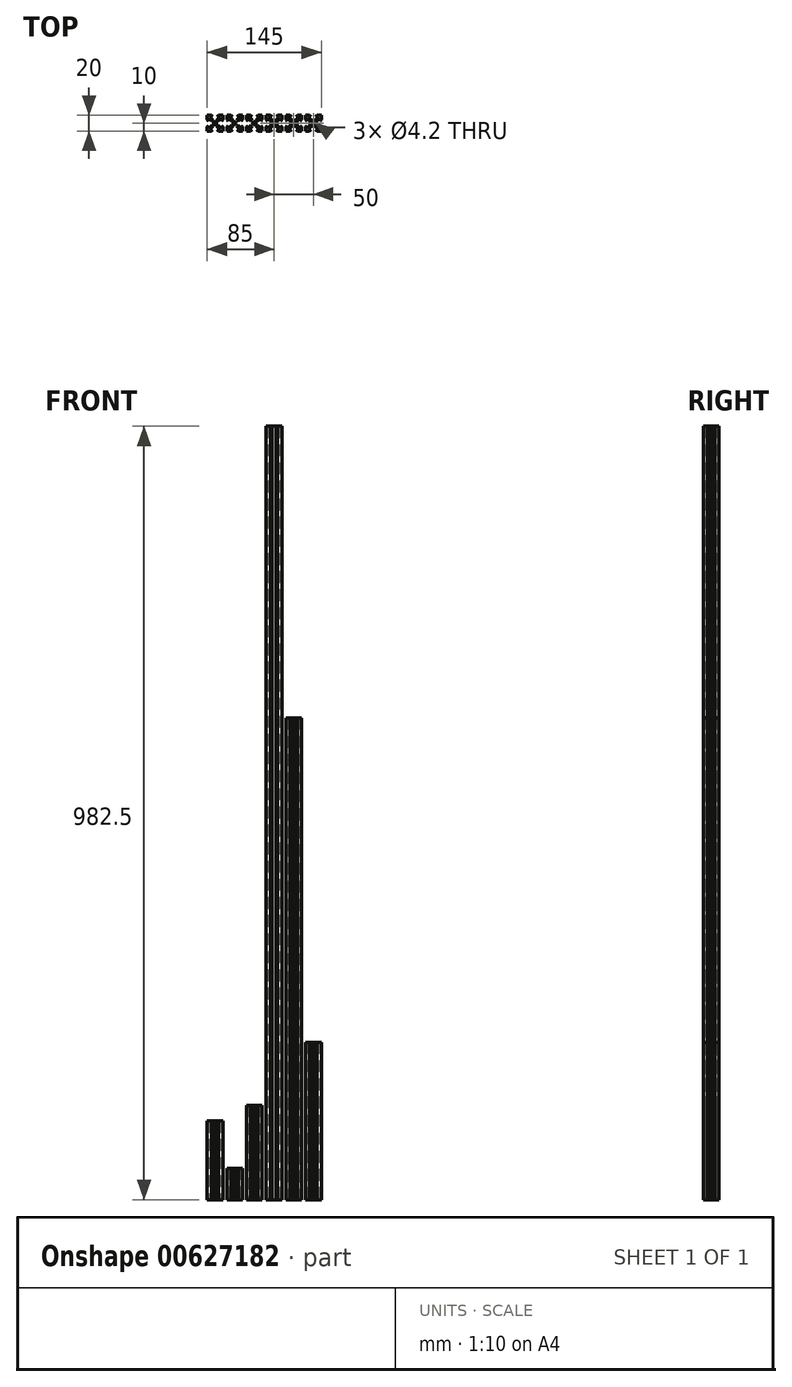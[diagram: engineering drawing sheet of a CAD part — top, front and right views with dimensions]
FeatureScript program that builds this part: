
annotation { "Feature Type Name" : "Feature", "Feature Type Description" : "" }
export const myFeature = defineFeature(function(context is Context, id is Id, definition is map)
    precondition{}
    {
        {
            var Q0;
            Q0=qCreatedBy(makeId("Top.planeOp"),FACE);
            var sketch = newSketch(context, id + "F0", { "sketchPlane" : qUnion([Q0])});
            skLineSegment(sketch, "E0.bottom", {"start": v(10, -10) * mm, "end": v(-10, -10) * mm});
            skLineSegment(sketch, "E0.top", {"start": v(10, 10) * mm, "end": v(-10, 10) * mm});
            skLineSegment(sketch, "E0.left", {"start": v(10, -10) * mm, "end": v(10, 10) * mm});
            skLineSegment(sketch, "E0.right", {"start": v(-10, -10) * mm, "end": v(-10, 10) * mm});
            skPoint(sketch, "E0.middle", {"position": v(0, 0) * mm});
            skCircle(sketch, "E1", {"center": v(0, 0) * mm, "radius": 2.1 * mm});
            skLineSegment(sketch, "E2.bottom", {"start": v(8.2, -8.2) * mm, "end": v(-8.2, -8.2) * mm});
            skLineSegment(sketch, "E2.top", {"start": v(8.2, 8.2) * mm, "end": v(-8.2, 8.2) * mm});
            skLineSegment(sketch, "E2.left", {"start": v(8.2, -8.2) * mm, "end": v(8.2, 8.2) * mm});
            skLineSegment(sketch, "E2.right", {"start": v(-8.2, -8.2) * mm, "end": v(-8.2, 8.2) * mm});
            skLineSegment(sketch, "E3", {"start": v(-8.2, 2.84) * mm, "end": v(-8.2, -2.84) * mm});
            skLineSegment(sketch, "E4", {"start": v(-8.2, 2.84) * mm, "end": v(-10, 4.64) * mm});
            skLineSegment(sketch, "E5", {"start": v(-10, 10) * mm, "end": v(10, -10) * mm, "construction": true});
            skLineSegment(sketch, "E6", {"start": v(10, 10) * mm, "end": v(-10, -10) * mm, "construction": true});
            skLineSegment(sketch, "E7", {"start": v(0, 10) * mm, "end": v(0, -10) * mm, "construction": true});
            skLineSegment(sketch, "E8", {"start": v(10, 0) * mm, "end": v(-10, 0) * mm, "construction": true});
            skLineSegment(sketch, "E9.MirrorCS", {"start": v(-2.84, 8.2) * mm, "end": v(-4.64, 10) * mm});
            skLineSegment(sketch, "E10.MirrorCS", {"start": v(2.84, -8.2) * mm, "end": v(4.64, -10) * mm});
            skLineSegment(sketch, "E11.MirrorCS", {"start": v(8.2, -2.84) * mm, "end": v(10, -4.64) * mm});
            skLineSegment(sketch, "E12.MirrorCS", {"start": v(2.84, 8.2) * mm, "end": v(4.64, 10) * mm});
            skLineSegment(sketch, "E13.MirrorCS", {"start": v(8.2, 2.84) * mm, "end": v(10, 4.64) * mm});
            skLineSegment(sketch, "E14.MirrorCS", {"start": v(-8.2, -2.84) * mm, "end": v(-10, -4.64) * mm});
            skLineSegment(sketch, "E15.MirrorCS", {"start": v(-2.84, -8.2) * mm, "end": v(-4.64, -10) * mm});
            skLineSegment(sketch, "E16.bottom", {"start": v(4, -4) * mm, "end": v(-4, -4) * mm});
            skLineSegment(sketch, "E16.top", {"start": v(4, 4) * mm, "end": v(-4, 4) * mm});
            skLineSegment(sketch, "E16.left", {"start": v(4, -4) * mm, "end": v(4, 4) * mm});
            skLineSegment(sketch, "E16.right", {"start": v(-4, -4) * mm, "end": v(-4, 4) * mm});
            skLineSegment(sketch, "E17", {"start": v(6.5, 8.2) * mm, "end": v(2.3, 4) * mm});
            skLineSegment(sketch, "E18.MirrorCS", {"start": v(8.2, 6.5) * mm, "end": v(4, 2.3) * mm});
            skLineSegment(sketch, "E19.MirrorCS", {"start": v(8.2, -6.5) * mm, "end": v(4, -2.3) * mm});
            skLineSegment(sketch, "E20.MirrorCS", {"start": v(6.5, -8.2) * mm, "end": v(2.3, -4) * mm});
            skLineSegment(sketch, "E21.MirrorCS", {"start": v(-6.5, -8.2) * mm, "end": v(-2.3, -4) * mm});
            skLineSegment(sketch, "E22.MirrorCS", {"start": v(-8.2, -6.5) * mm, "end": v(-4, -2.3) * mm});
            skLineSegment(sketch, "E23.MirrorCS", {"start": v(-6.5, 8.2) * mm, "end": v(-2.3, 4) * mm});
            skLineSegment(sketch, "E24.MirrorCS", {"start": v(-8.2, 6.5) * mm, "end": v(-4, 2.3) * mm});
            skLineSegment(sketch, "E25.1.0.0", {"start": v(33.2, 6.5) * mm, "end": v(29, 2.3) * mm});
            skLineSegment(sketch, "E25.1.0.1", {"start": v(35, -10) * mm, "end": v(15, -10) * mm});
            skLineSegment(sketch, "E25.1.0.2", {"start": v(15, -10) * mm, "end": v(15, 10) * mm});
            skLineSegment(sketch, "E25.1.0.3", {"start": v(18.5, -8.2) * mm, "end": v(22.7, -4) * mm});
            skLineSegment(sketch, "E25.1.0.4", {"start": v(21, -4) * mm, "end": v(21, 4) * mm});
            skLineSegment(sketch, "E25.1.0.5", {"start": v(16.8, 6.5) * mm, "end": v(21, 2.3) * mm});
            skPoint(sketch, "E25.1.0.6", {"position": v(25, 0) * mm});
            skLineSegment(sketch, "E25.1.0.7", {"start": v(16.8, -6.5) * mm, "end": v(21, -2.3) * mm});
            skLineSegment(sketch, "E25.1.0.8", {"start": v(25, 10) * mm, "end": v(25, -10) * mm, "construction": true});
            skLineSegment(sketch, "E25.1.0.9", {"start": v(35, -10) * mm, "end": v(35, 10) * mm});
            skLineSegment(sketch, "E25.1.0.10", {"start": v(35, 0) * mm, "end": v(15, 0) * mm, "construction": true});
            skLineSegment(sketch, "E25.1.0.11", {"start": v(35, 10) * mm, "end": v(15, 10) * mm});
            skLineSegment(sketch, "E25.1.0.12", {"start": v(16.8, -8.2) * mm, "end": v(16.8, 8.2) * mm});
            skLineSegment(sketch, "E25.1.0.13", {"start": v(33.2, 8.2) * mm, "end": v(16.8, 8.2) * mm});
            skLineSegment(sketch, "E25.1.0.14", {"start": v(16.8, -2.84) * mm, "end": v(15, -4.64) * mm});
            skLineSegment(sketch, "E25.1.0.15", {"start": v(18.5, 8.2) * mm, "end": v(22.7, 4) * mm});
            skLineSegment(sketch, "E25.1.0.16", {"start": v(29, 4) * mm, "end": v(21, 4) * mm});
            skLineSegment(sketch, "E25.1.0.17", {"start": v(33.2, -8.2) * mm, "end": v(33.2, 8.2) * mm});
            skLineSegment(sketch, "E25.1.0.18", {"start": v(16.8, 2.84) * mm, "end": v(16.8, -2.84) * mm});
            skLineSegment(sketch, "E25.1.0.19", {"start": v(29, -4) * mm, "end": v(29, 4) * mm});
            skLineSegment(sketch, "E25.1.0.20", {"start": v(33.2, -8.2) * mm, "end": v(16.8, -8.2) * mm});
            skLineSegment(sketch, "E25.1.0.21", {"start": v(35, 10) * mm, "end": v(15, -10) * mm, "construction": true});
            skLineSegment(sketch, "E25.1.0.22", {"start": v(33.2, -2.84) * mm, "end": v(35, -4.64) * mm});
            skLineSegment(sketch, "E25.1.0.23", {"start": v(31.5, -8.2) * mm, "end": v(27.3, -4) * mm});
            skCircle(sketch, "E25.1.0.24", {"center": v(25, 0) * mm, "radius": 2.1 * mm});
            skLineSegment(sketch, "E25.1.0.25", {"start": v(33.2, -6.5) * mm, "end": v(29, -2.3) * mm});
            skLineSegment(sketch, "E25.1.0.26", {"start": v(31.5, 8.2) * mm, "end": v(27.3, 4) * mm});
            skLineSegment(sketch, "E25.1.0.27", {"start": v(15, 10) * mm, "end": v(35, -10) * mm, "construction": true});
            skLineSegment(sketch, "E25.1.0.28", {"start": v(29, -4) * mm, "end": v(21, -4) * mm});
            skLineSegment(sketch, "E25.1.0.29", {"start": v(33.2, 2.84) * mm, "end": v(35, 4.64) * mm});
            skLineSegment(sketch, "E25.1.0.30", {"start": v(16.8, 2.84) * mm, "end": v(15, 4.64) * mm});
            skLineSegment(sketch, "E25.1.0.31", {"start": v(27.84, 8.2) * mm, "end": v(29.64, 10) * mm});
            skLineSegment(sketch, "E25.1.0.32", {"start": v(22.16, 8.2) * mm, "end": v(20.36, 10) * mm});
            skLineSegment(sketch, "E25.1.0.33", {"start": v(27.84, -8.2) * mm, "end": v(29.64, -10) * mm});
            skLineSegment(sketch, "E25.1.0.34", {"start": v(22.16, -8.2) * mm, "end": v(20.36, -10) * mm});
            skPoint(sketch, "E25.1.0.35", {"position": v(25, 0) * mm});
            skPoint(sketch, "E25.1.0.36", {"position": v(25, 0) * mm});
            skLineSegment(sketch, "E25.2.0.0", {"start": v(58.2, 6.5) * mm, "end": v(54, 2.3) * mm});
            skLineSegment(sketch, "E25.2.0.1", {"start": v(60, -10) * mm, "end": v(40, -10) * mm});
            skLineSegment(sketch, "E25.2.0.2", {"start": v(40, -10) * mm, "end": v(40, 10) * mm});
            skLineSegment(sketch, "E25.2.0.3", {"start": v(43.5, -8.2) * mm, "end": v(47.7, -4) * mm});
            skLineSegment(sketch, "E25.2.0.4", {"start": v(46, -4) * mm, "end": v(46, 4) * mm});
            skLineSegment(sketch, "E25.2.0.5", {"start": v(41.8, 6.5) * mm, "end": v(46, 2.3) * mm});
            skPoint(sketch, "E25.2.0.6", {"position": v(50, 0) * mm});
            skLineSegment(sketch, "E25.2.0.7", {"start": v(41.8, -6.5) * mm, "end": v(46, -2.3) * mm});
            skLineSegment(sketch, "E25.2.0.8", {"start": v(50, 10) * mm, "end": v(50, -10) * mm, "construction": true});
            skLineSegment(sketch, "E25.2.0.9", {"start": v(60, -10) * mm, "end": v(60, 10) * mm});
            skLineSegment(sketch, "E25.2.0.10", {"start": v(60, 0) * mm, "end": v(40, 0) * mm, "construction": true});
            skLineSegment(sketch, "E25.2.0.11", {"start": v(60, 10) * mm, "end": v(40, 10) * mm});
            skLineSegment(sketch, "E25.2.0.12", {"start": v(41.8, -8.2) * mm, "end": v(41.8, 8.2) * mm});
            skLineSegment(sketch, "E25.2.0.13", {"start": v(58.2, 8.2) * mm, "end": v(41.8, 8.2) * mm});
            skLineSegment(sketch, "E25.2.0.14", {"start": v(41.8, -2.84) * mm, "end": v(40, -4.64) * mm});
            skLineSegment(sketch, "E25.2.0.15", {"start": v(43.5, 8.2) * mm, "end": v(47.7, 4) * mm});
            skLineSegment(sketch, "E25.2.0.16", {"start": v(54, 4) * mm, "end": v(46, 4) * mm});
            skLineSegment(sketch, "E25.2.0.17", {"start": v(58.2, -8.2) * mm, "end": v(58.2, 8.2) * mm});
            skLineSegment(sketch, "E25.2.0.18", {"start": v(41.8, 2.84) * mm, "end": v(41.8, -2.84) * mm});
            skLineSegment(sketch, "E25.2.0.19", {"start": v(54, -4) * mm, "end": v(54, 4) * mm});
            skLineSegment(sketch, "E25.2.0.20", {"start": v(58.2, -8.2) * mm, "end": v(41.8, -8.2) * mm});
            skLineSegment(sketch, "E25.2.0.21", {"start": v(60, 10) * mm, "end": v(40, -10) * mm, "construction": true});
            skLineSegment(sketch, "E25.2.0.22", {"start": v(58.2, -2.84) * mm, "end": v(60, -4.64) * mm});
            skLineSegment(sketch, "E25.2.0.23", {"start": v(56.5, -8.2) * mm, "end": v(52.3, -4) * mm});
            skCircle(sketch, "E25.2.0.24", {"center": v(50, 0) * mm, "radius": 2.1 * mm});
            skLineSegment(sketch, "E25.2.0.25", {"start": v(58.2, -6.5) * mm, "end": v(54, -2.3) * mm});
            skLineSegment(sketch, "E25.2.0.26", {"start": v(56.5, 8.2) * mm, "end": v(52.3, 4) * mm});
            skLineSegment(sketch, "E25.2.0.27", {"start": v(40, 10) * mm, "end": v(60, -10) * mm, "construction": true});
            skLineSegment(sketch, "E25.2.0.28", {"start": v(54, -4) * mm, "end": v(46, -4) * mm});
            skLineSegment(sketch, "E25.2.0.29", {"start": v(58.2, 2.84) * mm, "end": v(60, 4.64) * mm});
            skLineSegment(sketch, "E25.2.0.30", {"start": v(41.8, 2.84) * mm, "end": v(40, 4.64) * mm});
            skLineSegment(sketch, "E25.2.0.31", {"start": v(52.84, 8.2) * mm, "end": v(54.64, 10) * mm});
            skLineSegment(sketch, "E25.2.0.32", {"start": v(47.16, 8.2) * mm, "end": v(45.36, 10) * mm});
            skLineSegment(sketch, "E25.2.0.33", {"start": v(52.84, -8.2) * mm, "end": v(54.64, -10) * mm});
            skLineSegment(sketch, "E25.2.0.34", {"start": v(47.16, -8.2) * mm, "end": v(45.36, -10) * mm});
            skPoint(sketch, "E25.2.0.35", {"position": v(50, 0) * mm});
            skPoint(sketch, "E25.2.0.36", {"position": v(50, 0) * mm});
            skLineSegment(sketch, "E25.3.0.0", {"start": v(83.2, 6.5) * mm, "end": v(79, 2.3) * mm});
            skLineSegment(sketch, "E25.3.0.1", {"start": v(85, -10) * mm, "end": v(65, -10) * mm});
            skLineSegment(sketch, "E25.3.0.2", {"start": v(65, -10) * mm, "end": v(65, 10) * mm});
            skLineSegment(sketch, "E25.3.0.3", {"start": v(68.5, -8.2) * mm, "end": v(72.7, -4) * mm});
            skLineSegment(sketch, "E25.3.0.4", {"start": v(71, -4) * mm, "end": v(71, 4) * mm});
            skLineSegment(sketch, "E25.3.0.5", {"start": v(66.8, 6.5) * mm, "end": v(71, 2.3) * mm});
            skPoint(sketch, "E25.3.0.6", {"position": v(75, 0) * mm});
            skLineSegment(sketch, "E25.3.0.7", {"start": v(66.8, -6.5) * mm, "end": v(71, -2.3) * mm});
            skLineSegment(sketch, "E25.3.0.8", {"start": v(75, 10) * mm, "end": v(75, -10) * mm, "construction": true});
            skLineSegment(sketch, "E25.3.0.9", {"start": v(85, -10) * mm, "end": v(85, 10) * mm});
            skLineSegment(sketch, "E25.3.0.10", {"start": v(85, 0) * mm, "end": v(65, 0) * mm, "construction": true});
            skLineSegment(sketch, "E25.3.0.11", {"start": v(85, 10) * mm, "end": v(65, 10) * mm});
            skLineSegment(sketch, "E25.3.0.12", {"start": v(66.8, -8.2) * mm, "end": v(66.8, 8.2) * mm});
            skLineSegment(sketch, "E25.3.0.13", {"start": v(83.2, 8.2) * mm, "end": v(66.8, 8.2) * mm});
            skLineSegment(sketch, "E25.3.0.14", {"start": v(66.8, -2.84) * mm, "end": v(65, -4.64) * mm});
            skLineSegment(sketch, "E25.3.0.15", {"start": v(68.5, 8.2) * mm, "end": v(72.7, 4) * mm});
            skLineSegment(sketch, "E25.3.0.16", {"start": v(79, 4) * mm, "end": v(71, 4) * mm});
            skLineSegment(sketch, "E25.3.0.17", {"start": v(83.2, -8.2) * mm, "end": v(83.2, 8.2) * mm});
            skLineSegment(sketch, "E25.3.0.18", {"start": v(66.8, 2.84) * mm, "end": v(66.8, -2.84) * mm});
            skLineSegment(sketch, "E25.3.0.19", {"start": v(79, -4) * mm, "end": v(79, 4) * mm});
            skLineSegment(sketch, "E25.3.0.20", {"start": v(83.2, -8.2) * mm, "end": v(66.8, -8.2) * mm});
            skLineSegment(sketch, "E25.3.0.21", {"start": v(85, 10) * mm, "end": v(65, -10) * mm, "construction": true});
            skLineSegment(sketch, "E25.3.0.22", {"start": v(83.2, -2.84) * mm, "end": v(85, -4.64) * mm});
            skLineSegment(sketch, "E25.3.0.23", {"start": v(81.5, -8.2) * mm, "end": v(77.3, -4) * mm});
            skCircle(sketch, "E25.3.0.24", {"center": v(75, 0) * mm, "radius": 2.1 * mm});
            skLineSegment(sketch, "E25.3.0.25", {"start": v(83.2, -6.5) * mm, "end": v(79, -2.3) * mm});
            skLineSegment(sketch, "E25.3.0.26", {"start": v(81.5, 8.2) * mm, "end": v(77.3, 4) * mm});
            skLineSegment(sketch, "E25.3.0.27", {"start": v(65, 10) * mm, "end": v(85, -10) * mm, "construction": true});
            skLineSegment(sketch, "E25.3.0.28", {"start": v(79, -4) * mm, "end": v(71, -4) * mm});
            skLineSegment(sketch, "E25.3.0.29", {"start": v(83.2, 2.84) * mm, "end": v(85, 4.64) * mm});
            skLineSegment(sketch, "E25.3.0.30", {"start": v(66.8, 2.84) * mm, "end": v(65, 4.64) * mm});
            skLineSegment(sketch, "E25.3.0.31", {"start": v(77.84, 8.2) * mm, "end": v(79.64, 10) * mm});
            skLineSegment(sketch, "E25.3.0.32", {"start": v(72.16, 8.2) * mm, "end": v(70.36, 10) * mm});
            skLineSegment(sketch, "E25.3.0.33", {"start": v(77.84, -8.2) * mm, "end": v(79.64, -10) * mm});
            skLineSegment(sketch, "E25.3.0.34", {"start": v(72.16, -8.2) * mm, "end": v(70.36, -10) * mm});
            skPoint(sketch, "E25.3.0.35", {"position": v(75, 0) * mm});
            skPoint(sketch, "E25.3.0.36", {"position": v(75, 0) * mm});
            skLineSegment(sketch, "E25.4.0.0", {"start": v(108.2, 6.5) * mm, "end": v(104, 2.3) * mm});
            skLineSegment(sketch, "E25.4.0.1", {"start": v(110, -10) * mm, "end": v(90, -10) * mm});
            skLineSegment(sketch, "E25.4.0.2", {"start": v(90, -10) * mm, "end": v(90, 10) * mm});
            skLineSegment(sketch, "E25.4.0.3", {"start": v(93.5, -8.2) * mm, "end": v(97.7, -4) * mm});
            skLineSegment(sketch, "E25.4.0.4", {"start": v(96, -4) * mm, "end": v(96, 4) * mm});
            skLineSegment(sketch, "E25.4.0.5", {"start": v(91.8, 6.5) * mm, "end": v(96, 2.3) * mm});
            skPoint(sketch, "E25.4.0.6", {"position": v(100, 0) * mm});
            skLineSegment(sketch, "E25.4.0.7", {"start": v(91.8, -6.5) * mm, "end": v(96, -2.3) * mm});
            skLineSegment(sketch, "E25.4.0.8", {"start": v(100, 10) * mm, "end": v(100, -10) * mm, "construction": true});
            skLineSegment(sketch, "E25.4.0.9", {"start": v(110, -10) * mm, "end": v(110, 10) * mm});
            skLineSegment(sketch, "E25.4.0.10", {"start": v(110, 0) * mm, "end": v(90, 0) * mm, "construction": true});
            skLineSegment(sketch, "E25.4.0.11", {"start": v(110, 10) * mm, "end": v(90, 10) * mm});
            skLineSegment(sketch, "E25.4.0.12", {"start": v(91.8, -8.2) * mm, "end": v(91.8, 8.2) * mm});
            skLineSegment(sketch, "E25.4.0.13", {"start": v(108.2, 8.2) * mm, "end": v(91.8, 8.2) * mm});
            skLineSegment(sketch, "E25.4.0.14", {"start": v(91.8, -2.84) * mm, "end": v(90, -4.64) * mm});
            skLineSegment(sketch, "E25.4.0.15", {"start": v(93.5, 8.2) * mm, "end": v(97.7, 4) * mm});
            skLineSegment(sketch, "E25.4.0.16", {"start": v(104, 4) * mm, "end": v(96, 4) * mm});
            skLineSegment(sketch, "E25.4.0.17", {"start": v(108.2, -8.2) * mm, "end": v(108.2, 8.2) * mm});
            skLineSegment(sketch, "E25.4.0.18", {"start": v(91.8, 2.84) * mm, "end": v(91.8, -2.84) * mm});
            skLineSegment(sketch, "E25.4.0.19", {"start": v(104, -4) * mm, "end": v(104, 4) * mm});
            skLineSegment(sketch, "E25.4.0.20", {"start": v(108.2, -8.2) * mm, "end": v(91.8, -8.2) * mm});
            skLineSegment(sketch, "E25.4.0.21", {"start": v(110, 10) * mm, "end": v(90, -10) * mm, "construction": true});
            skLineSegment(sketch, "E25.4.0.22", {"start": v(108.2, -2.84) * mm, "end": v(110, -4.64) * mm});
            skLineSegment(sketch, "E25.4.0.23", {"start": v(106.5, -8.2) * mm, "end": v(102.3, -4) * mm});
            skCircle(sketch, "E25.4.0.24", {"center": v(100, 0) * mm, "radius": 2.1 * mm});
            skLineSegment(sketch, "E25.4.0.25", {"start": v(108.2, -6.5) * mm, "end": v(104, -2.3) * mm});
            skLineSegment(sketch, "E25.4.0.26", {"start": v(106.5, 8.2) * mm, "end": v(102.3, 4) * mm});
            skLineSegment(sketch, "E25.4.0.27", {"start": v(90, 10) * mm, "end": v(110, -10) * mm, "construction": true});
            skLineSegment(sketch, "E25.4.0.28", {"start": v(104, -4) * mm, "end": v(96, -4) * mm});
            skLineSegment(sketch, "E25.4.0.29", {"start": v(108.2, 2.84) * mm, "end": v(110, 4.64) * mm});
            skLineSegment(sketch, "E25.4.0.30", {"start": v(91.8, 2.84) * mm, "end": v(90, 4.64) * mm});
            skLineSegment(sketch, "E25.4.0.31", {"start": v(102.84, 8.2) * mm, "end": v(104.64, 10) * mm});
            skLineSegment(sketch, "E25.4.0.32", {"start": v(97.16, 8.2) * mm, "end": v(95.36, 10) * mm});
            skLineSegment(sketch, "E25.4.0.33", {"start": v(102.84, -8.2) * mm, "end": v(104.64, -10) * mm});
            skLineSegment(sketch, "E25.4.0.34", {"start": v(97.16, -8.2) * mm, "end": v(95.36, -10) * mm});
            skPoint(sketch, "E25.4.0.35", {"position": v(100, 0) * mm});
            skPoint(sketch, "E25.4.0.36", {"position": v(100, 0) * mm});
            skLineSegment(sketch, "E25.direction1", {"start": v(-10, -10) * mm, "end": v(15, -10) * mm, "construction": true});
            skLineSegment(sketch, "E26", {"start": v(-12.5, 5) * mm, "end": v(-12.5, -5) * mm, "construction": true});
            skLineSegment(sketch, "E27.MirrorCS", {"start": v(-16.8, -2.84) * mm, "end": v(-15, -4.64) * mm});
            skCircle(sketch, "E28.MirrorC", {"center": v(-50, 0) * mm, "radius": 2.1 * mm});
            skCircle(sketch, "E29.MirrorC", {"center": v(-125, 0) * mm, "radius": 2.1 * mm});
            skCircle(sketch, "E30.MirrorC", {"center": v(-25, 0) * mm, "radius": 2.1 * mm});
            skCircle(sketch, "E31.MirrorC", {"center": v(-100, 0) * mm, "radius": 2.1 * mm});
            skCircle(sketch, "E32.MirrorC", {"center": v(-75, 0) * mm, "radius": 2.1 * mm});
            skLineSegment(sketch, "E33.MirrorCS", {"start": v(-66.8, 2.84) * mm, "end": v(-66.8, -2.84) * mm});
            skLineSegment(sketch, "E34.MirrorCS", {"start": v(-91.8, 2.84) * mm, "end": v(-90, 4.64) * mm});
            skLineSegment(sketch, "E35.MirrorCS", {"start": v(-41.8, -2.84) * mm, "end": v(-40, -4.64) * mm});
            skLineSegment(sketch, "E36.MirrorCS", {"start": v(-66.8, 2.84) * mm, "end": v(-65, 4.64) * mm});
            skLineSegment(sketch, "E37.MirrorCS", {"start": v(-41.8, 2.84) * mm, "end": v(-40, 4.64) * mm});
            skLineSegment(sketch, "E38.MirrorCS", {"start": v(-16.8, 2.84) * mm, "end": v(-15, 4.64) * mm});
            skLineSegment(sketch, "E39.MirrorCS", {"start": v(-66.8, -2.84) * mm, "end": v(-65, -4.64) * mm});
            skLineSegment(sketch, "E40.MirrorCS", {"start": v(-41.8, -6.5) * mm, "end": v(-46, -2.3) * mm});
            skLineSegment(sketch, "E41.MirrorCS", {"start": v(-41.8, 2.84) * mm, "end": v(-41.8, -2.84) * mm});
            skLineSegment(sketch, "E42.MirrorCS", {"start": v(-116.8, -2.84) * mm, "end": v(-115, -4.64) * mm});
            skLineSegment(sketch, "E43.MirrorCS", {"start": v(-116.8, 2.84) * mm, "end": v(-115, 4.64) * mm});
            skLineSegment(sketch, "E44.MirrorCS", {"start": v(-52.84, -8.2) * mm, "end": v(-54.64, -10) * mm});
            skLineSegment(sketch, "E45.MirrorCS", {"start": v(-47.16, -8.2) * mm, "end": v(-45.36, -10) * mm});
            skLineSegment(sketch, "E46.MirrorCS", {"start": v(-33.2, -2.84) * mm, "end": v(-35, -4.64) * mm});
            skLineSegment(sketch, "E47.MirrorCS", {"start": v(-97.16, -8.2) * mm, "end": v(-95.36, -10) * mm});
            skLineSegment(sketch, "E48.MirrorCS", {"start": v(-104, 4) * mm, "end": v(-96, 4) * mm});
            skLineSegment(sketch, "E49.MirrorCS", {"start": v(-58.2, 8.2) * mm, "end": v(-41.8, 8.2) * mm});
            skLineSegment(sketch, "E50.MirrorCS", {"start": v(-135, 10) * mm, "end": v(-115, -10) * mm, "construction": true});
            skLineSegment(sketch, "E51.MirrorCS", {"start": v(-83.2, 8.2) * mm, "end": v(-66.8, 8.2) * mm});
            skLineSegment(sketch, "E52.MirrorCS", {"start": v(-129, 4) * mm, "end": v(-121, 4) * mm});
            skLineSegment(sketch, "E53.MirrorCS", {"start": v(-41.8, -8.2) * mm, "end": v(-41.8, 8.2) * mm});
            skLineSegment(sketch, "E54.MirrorCS", {"start": v(-33.2, -8.2) * mm, "end": v(-33.2, 8.2) * mm});
            skLineSegment(sketch, "E55.MirrorCS", {"start": v(-108.2, -8.2) * mm, "end": v(-91.8, -8.2) * mm});
            skLineSegment(sketch, "E56.MirrorCS", {"start": v(-33.2, -8.2) * mm, "end": v(-16.8, -8.2) * mm});
            skLineSegment(sketch, "E57.MirrorCS", {"start": v(-81.5, -8.2) * mm, "end": v(-77.3, -4) * mm});
            skLineSegment(sketch, "E58.MirrorCS", {"start": v(-133.2, -8.2) * mm, "end": v(-116.8, -8.2) * mm});
            skLineSegment(sketch, "E59.MirrorCS", {"start": v(-16.8, 2.84) * mm, "end": v(-16.8, -2.84) * mm});
            skLineSegment(sketch, "E60.MirrorCS", {"start": v(-72.16, -8.2) * mm, "end": v(-70.36, -10) * mm});
            skLineSegment(sketch, "E61.MirrorCS", {"start": v(-35, -10) * mm, "end": v(-35, 10) * mm});
            skLineSegment(sketch, "E62.MirrorCS", {"start": v(-18.5, 8.2) * mm, "end": v(-22.7, 4) * mm});
            skLineSegment(sketch, "E63.MirrorCS", {"start": v(-116.8, -6.5) * mm, "end": v(-121, -2.3) * mm});
            skLineSegment(sketch, "E64.MirrorCS", {"start": v(-31.5, -8.2) * mm, "end": v(-27.3, -4) * mm});
            skLineSegment(sketch, "E65.MirrorCS", {"start": v(-33.2, -6.5) * mm, "end": v(-29, -2.3) * mm});
            skLineSegment(sketch, "E66.MirrorCS", {"start": v(-54, 4) * mm, "end": v(-46, 4) * mm});
            skLineSegment(sketch, "E67.MirrorCS", {"start": v(-91.8, -2.84) * mm, "end": v(-90, -4.64) * mm});
            skLineSegment(sketch, "E68.MirrorCS", {"start": v(-22.16, -8.2) * mm, "end": v(-20.36, -10) * mm});
            skLineSegment(sketch, "E69.MirrorCS", {"start": v(-83.2, -6.5) * mm, "end": v(-79, -2.3) * mm});
            skLineSegment(sketch, "E70.MirrorCS", {"start": v(-77.84, 8.2) * mm, "end": v(-79.64, 10) * mm});
            skLineSegment(sketch, "E71.MirrorCS", {"start": v(-115, 10) * mm, "end": v(-135, -10) * mm, "construction": true});
            skLineSegment(sketch, "E72.MirrorCS", {"start": v(-27.84, -8.2) * mm, "end": v(-29.64, -10) * mm});
            skLineSegment(sketch, "E73.MirrorCS", {"start": v(-58.2, -2.84) * mm, "end": v(-60, -4.64) * mm});
            skLineSegment(sketch, "E74.MirrorCS", {"start": v(-68.5, 8.2) * mm, "end": v(-72.7, 4) * mm});
            skLineSegment(sketch, "E75.MirrorCS", {"start": v(-133.2, 8.2) * mm, "end": v(-116.8, 8.2) * mm});
            skLineSegment(sketch, "E76.MirrorCS", {"start": v(-16.8, 6.5) * mm, "end": v(-21, 2.3) * mm});
            skLineSegment(sketch, "E77.MirrorCS", {"start": v(-135, -10) * mm, "end": v(-135, 10) * mm});
            skLineSegment(sketch, "E78.MirrorCS", {"start": v(-58.2, -8.2) * mm, "end": v(-41.8, -8.2) * mm});
            skLineSegment(sketch, "E79.MirrorCS", {"start": v(-47.16, 8.2) * mm, "end": v(-45.36, 10) * mm});
            skLineSegment(sketch, "E80.MirrorCS", {"start": v(-79, -4) * mm, "end": v(-79, 4) * mm});
            skLineSegment(sketch, "E81.MirrorCS", {"start": v(-21, -4) * mm, "end": v(-21, 4) * mm});
            skLineSegment(sketch, "E82.MirrorCS", {"start": v(-93.5, -8.2) * mm, "end": v(-97.7, -4) * mm});
            skLineSegment(sketch, "E83.MirrorCS", {"start": v(-108.2, -2.84) * mm, "end": v(-110, -4.64) * mm});
            skLineSegment(sketch, "E84.MirrorCS", {"start": v(-83.2, -2.84) * mm, "end": v(-85, -4.64) * mm});
            skLineSegment(sketch, "E85.MirrorCS", {"start": v(-133.2, 2.84) * mm, "end": v(-135, 4.64) * mm});
            skLineSegment(sketch, "E86.MirrorCS", {"start": v(-108.2, 2.84) * mm, "end": v(-110, 4.64) * mm});
            skLineSegment(sketch, "E87.MirrorCS", {"start": v(-102.84, 8.2) * mm, "end": v(-104.64, 10) * mm});
            skLineSegment(sketch, "E88.MirrorCS", {"start": v(-56.5, 8.2) * mm, "end": v(-52.3, 4) * mm});
            skLineSegment(sketch, "E89.MirrorCS", {"start": v(-56.5, -8.2) * mm, "end": v(-52.3, -4) * mm});
            skLineSegment(sketch, "E90.MirrorCS", {"start": v(-33.2, 8.2) * mm, "end": v(-16.8, 8.2) * mm});
            skLineSegment(sketch, "E91.MirrorCS", {"start": v(-77.84, -8.2) * mm, "end": v(-79.64, -10) * mm});
            skLineSegment(sketch, "E92.MirrorCS", {"start": v(-91.8, 2.84) * mm, "end": v(-91.8, -2.84) * mm});
            skLineSegment(sketch, "E93.MirrorCS", {"start": v(-116.8, 6.5) * mm, "end": v(-121, 2.3) * mm});
            skLineSegment(sketch, "E94.MirrorCS", {"start": v(-118.5, -8.2) * mm, "end": v(-122.7, -4) * mm});
            skLineSegment(sketch, "E95.MirrorCS", {"start": v(-131.5, 8.2) * mm, "end": v(-127.3, 4) * mm});
            skLineSegment(sketch, "E96.MirrorCS", {"start": v(-29, -4) * mm, "end": v(-21, -4) * mm});
            skLineSegment(sketch, "E97.MirrorCS", {"start": v(-83.2, -8.2) * mm, "end": v(-66.8, -8.2) * mm});
            skLineSegment(sketch, "E98.MirrorCS", {"start": v(-121, -4) * mm, "end": v(-121, 4) * mm});
            skLineSegment(sketch, "E99.MirrorCS", {"start": v(-43.5, 8.2) * mm, "end": v(-47.7, 4) * mm});
            skLineSegment(sketch, "E100.MirrorCS", {"start": v(-81.5, 8.2) * mm, "end": v(-77.3, 4) * mm});
            skLineSegment(sketch, "E101.MirrorCS", {"start": v(-102.84, -8.2) * mm, "end": v(-104.64, -10) * mm});
            skLineSegment(sketch, "E102.MirrorCS", {"start": v(-131.5, -8.2) * mm, "end": v(-127.3, -4) * mm});
            skLineSegment(sketch, "E103.MirrorCS", {"start": v(-133.2, 6.5) * mm, "end": v(-129, 2.3) * mm});
            skLineSegment(sketch, "E104.MirrorCS", {"start": v(-18.5, -8.2) * mm, "end": v(-22.7, -4) * mm});
            skLineSegment(sketch, "E105.MirrorCS", {"start": v(-72.16, 8.2) * mm, "end": v(-70.36, 10) * mm});
            skLineSegment(sketch, "E106.MirrorCS", {"start": v(-33.2, 2.84) * mm, "end": v(-35, 4.64) * mm});
            skLineSegment(sketch, "E107.MirrorCS", {"start": v(-133.2, -6.5) * mm, "end": v(-129, -2.3) * mm});
            skLineSegment(sketch, "E108.MirrorCS", {"start": v(-122.16, -8.2) * mm, "end": v(-120.36, -10) * mm});
            skLineSegment(sketch, "E109.MirrorCS", {"start": v(-110, -10) * mm, "end": v(-110, 10) * mm});
            skLineSegment(sketch, "E110.MirrorCS", {"start": v(-91.8, 6.5) * mm, "end": v(-96, 2.3) * mm});
            skLineSegment(sketch, "E111.MirrorCS", {"start": v(-118.5, 8.2) * mm, "end": v(-122.7, 4) * mm});
            skLineSegment(sketch, "E112.MirrorCS", {"start": v(-129, -4) * mm, "end": v(-121, -4) * mm});
            skLineSegment(sketch, "E113.MirrorCS", {"start": v(-66.8, -8.2) * mm, "end": v(-66.8, 8.2) * mm});
            skLineSegment(sketch, "E114.MirrorCS", {"start": v(-68.5, -8.2) * mm, "end": v(-72.7, -4) * mm});
            skLineSegment(sketch, "E115.MirrorCS", {"start": v(-108.2, 8.2) * mm, "end": v(-91.8, 8.2) * mm});
            skLineSegment(sketch, "E116.MirrorCS", {"start": v(-122.16, 8.2) * mm, "end": v(-120.36, 10) * mm});
            skLineSegment(sketch, "E117.MirrorCS", {"start": v(-40, -10) * mm, "end": v(-40, 10) * mm});
            skLineSegment(sketch, "E118.MirrorCS", {"start": v(-52.84, 8.2) * mm, "end": v(-54.64, 10) * mm});
            skLineSegment(sketch, "E119.MirrorCS", {"start": v(-104, -4) * mm, "end": v(-96, -4) * mm});
            skLineSegment(sketch, "E120.MirrorCS", {"start": v(-96, -4) * mm, "end": v(-96, 4) * mm});
            skLineSegment(sketch, "E121.MirrorCS", {"start": v(-106.5, -8.2) * mm, "end": v(-102.3, -4) * mm});
            skLineSegment(sketch, "E122.MirrorCS", {"start": v(-97.16, 8.2) * mm, "end": v(-95.36, 10) * mm});
            skLineSegment(sketch, "E123.MirrorCS", {"start": v(-54, -4) * mm, "end": v(-46, -4) * mm});
            skLineSegment(sketch, "E124.MirrorCS", {"start": v(-35, -10) * mm, "end": v(-15, -10) * mm});
            skLineSegment(sketch, "E125.MirrorCS", {"start": v(-46, -4) * mm, "end": v(-46, 4) * mm});
            skLineSegment(sketch, "E126.MirrorCS", {"start": v(-108.2, -8.2) * mm, "end": v(-108.2, 8.2) * mm});
            skLineSegment(sketch, "E127.MirrorCS", {"start": v(-133.2, -2.84) * mm, "end": v(-135, -4.64) * mm});
            skLineSegment(sketch, "E128.MirrorCS", {"start": v(-16.8, -6.5) * mm, "end": v(-21, -2.3) * mm});
            skLineSegment(sketch, "E129.MirrorCS", {"start": v(-29, 4) * mm, "end": v(-21, 4) * mm});
            skLineSegment(sketch, "E130.MirrorCS", {"start": v(-127.84, -8.2) * mm, "end": v(-129.64, -10) * mm});
            skLineSegment(sketch, "E131.MirrorCS", {"start": v(-79, -4) * mm, "end": v(-71, -4) * mm});
            skLineSegment(sketch, "E132.MirrorCS", {"start": v(-54, -4) * mm, "end": v(-54, 4) * mm});
            skLineSegment(sketch, "E133.MirrorCS", {"start": v(-65, -10) * mm, "end": v(-65, 10) * mm});
            skLineSegment(sketch, "E134.MirrorCS", {"start": v(-58.2, -6.5) * mm, "end": v(-54, -2.3) * mm});
            skLineSegment(sketch, "E135.MirrorCS", {"start": v(-43.5, -8.2) * mm, "end": v(-47.7, -4) * mm});
            skLineSegment(sketch, "E136.MirrorCS", {"start": v(-91.8, -6.5) * mm, "end": v(-96, -2.3) * mm});
            skLineSegment(sketch, "E137.MirrorCS", {"start": v(-29, -4) * mm, "end": v(-29, 4) * mm});
            skLineSegment(sketch, "E138.MirrorCS", {"start": v(-127.84, 8.2) * mm, "end": v(-129.64, 10) * mm});
            skLineSegment(sketch, "E139.MirrorCS", {"start": v(-15, 10) * mm, "end": v(-35, -10) * mm, "construction": true});
            skLineSegment(sketch, "E140.MirrorCS", {"start": v(-31.5, 8.2) * mm, "end": v(-27.3, 4) * mm});
            skLineSegment(sketch, "E141.MirrorCS", {"start": v(-83.2, 6.5) * mm, "end": v(-79, 2.3) * mm});
            skLineSegment(sketch, "E142.MirrorCS", {"start": v(-106.5, 8.2) * mm, "end": v(-102.3, 4) * mm});
            skLineSegment(sketch, "E143.MirrorCS", {"start": v(-93.5, 8.2) * mm, "end": v(-97.7, 4) * mm});
            skLineSegment(sketch, "E144.MirrorCS", {"start": v(-133.2, -8.2) * mm, "end": v(-133.2, 8.2) * mm});
            skLineSegment(sketch, "E145.MirrorCS", {"start": v(-83.2, 2.84) * mm, "end": v(-85, 4.64) * mm});
            skLineSegment(sketch, "E146.MirrorCS", {"start": v(-16.8, -8.2) * mm, "end": v(-16.8, 8.2) * mm});
            skLineSegment(sketch, "E147.MirrorCS", {"start": v(-129, -4) * mm, "end": v(-129, 4) * mm});
            skLineSegment(sketch, "E148.MirrorCS", {"start": v(-116.8, -8.2) * mm, "end": v(-116.8, 8.2) * mm});
            skLineSegment(sketch, "E149.MirrorCS", {"start": v(-71, -4) * mm, "end": v(-71, 4) * mm});
            skLineSegment(sketch, "E150.MirrorCS", {"start": v(-22.16, 8.2) * mm, "end": v(-20.36, 10) * mm});
            skLineSegment(sketch, "E151.MirrorCS", {"start": v(-27.84, 8.2) * mm, "end": v(-29.64, 10) * mm});
            skLineSegment(sketch, "E152.MirrorCS", {"start": v(-40, 10) * mm, "end": v(-60, -10) * mm, "construction": true});
            skLineSegment(sketch, "E153.MirrorCS", {"start": v(-104, -4) * mm, "end": v(-104, 4) * mm});
            skLineSegment(sketch, "E154.MirrorCS", {"start": v(-33.2, 6.5) * mm, "end": v(-29, 2.3) * mm});
            skLineSegment(sketch, "E155.MirrorCS", {"start": v(-79, 4) * mm, "end": v(-71, 4) * mm});
            skLineSegment(sketch, "E156.MirrorCS", {"start": v(-58.2, 6.5) * mm, "end": v(-54, 2.3) * mm});
            skLineSegment(sketch, "E157.MirrorCS", {"start": v(-35, 10) * mm, "end": v(-15, -10) * mm, "construction": true});
            skLineSegment(sketch, "E158.MirrorCS", {"start": v(-41.8, 6.5) * mm, "end": v(-46, 2.3) * mm});
            skLineSegment(sketch, "E159.MirrorCS", {"start": v(-60, 10) * mm, "end": v(-40, -10) * mm, "construction": true});
            skLineSegment(sketch, "E160.MirrorCS", {"start": v(-58.2, 2.84) * mm, "end": v(-60, 4.64) * mm});
            skLineSegment(sketch, "E161.MirrorCS", {"start": v(-108.2, 6.5) * mm, "end": v(-104, 2.3) * mm});
            skLineSegment(sketch, "E162.MirrorCS", {"start": v(-35, 0) * mm, "end": v(-15, 0) * mm, "construction": true});
            skLineSegment(sketch, "E163.MirrorCS", {"start": v(-115, -10) * mm, "end": v(-115, 10) * mm});
            skLineSegment(sketch, "E164.MirrorCS", {"start": v(-66.8, -6.5) * mm, "end": v(-71, -2.3) * mm});
            skLineSegment(sketch, "E165.MirrorCS", {"start": v(-85, 10) * mm, "end": v(-65, -10) * mm, "construction": true});
            skLineSegment(sketch, "E166.MirrorCS", {"start": v(-66.8, 6.5) * mm, "end": v(-71, 2.3) * mm});
            skLineSegment(sketch, "E167.MirrorCS", {"start": v(-110, -10) * mm, "end": v(-90, -10) * mm});
            skLineSegment(sketch, "E168.MirrorCS", {"start": v(-15, -10) * mm, "end": v(-15, 10) * mm});
            skLineSegment(sketch, "E169.MirrorCS", {"start": v(-110, 10) * mm, "end": v(-90, -10) * mm, "construction": true});
            skLineSegment(sketch, "E170.MirrorCS", {"start": v(-65, 10) * mm, "end": v(-85, -10) * mm, "construction": true});
            skLineSegment(sketch, "E171.MirrorCS", {"start": v(-91.8, -8.2) * mm, "end": v(-91.8, 8.2) * mm});
            skLineSegment(sketch, "E172.MirrorCS", {"start": v(-60, -10) * mm, "end": v(-40, -10) * mm});
            skLineSegment(sketch, "E173.MirrorCS", {"start": v(-85, 0) * mm, "end": v(-65, 0) * mm, "construction": true});
            skLineSegment(sketch, "E174.MirrorCS", {"start": v(-108.2, -6.5) * mm, "end": v(-104, -2.3) * mm});
            skLineSegment(sketch, "E175.MirrorCS", {"start": v(-75, 10) * mm, "end": v(-75, -10) * mm, "construction": true});
            skLineSegment(sketch, "E176.MirrorCS", {"start": v(-135, -10) * mm, "end": v(-115, -10) * mm});
            skLineSegment(sketch, "E177.MirrorCS", {"start": v(-100, 10) * mm, "end": v(-100, -10) * mm, "construction": true});
            skLineSegment(sketch, "E178.MirrorCS", {"start": v(-50, 10) * mm, "end": v(-50, -10) * mm, "construction": true});
            skLineSegment(sketch, "E179.MirrorCS", {"start": v(-135, 0) * mm, "end": v(-115, 0) * mm, "construction": true});
            skLineSegment(sketch, "E180.MirrorCS", {"start": v(-58.2, -8.2) * mm, "end": v(-58.2, 8.2) * mm});
            skLineSegment(sketch, "E181.MirrorCS", {"start": v(-125, 10) * mm, "end": v(-125, -10) * mm, "construction": true});
            skLineSegment(sketch, "E182.MirrorCS", {"start": v(-15, -10) * mm, "end": v(-40, -10) * mm, "construction": true});
            skLineSegment(sketch, "E183.MirrorCS", {"start": v(-85, -10) * mm, "end": v(-85, 10) * mm});
            skLineSegment(sketch, "E184.MirrorCS", {"start": v(-85, 10) * mm, "end": v(-65, 10) * mm});
            skLineSegment(sketch, "E185.MirrorCS", {"start": v(-83.2, -8.2) * mm, "end": v(-83.2, 8.2) * mm});
            skLineSegment(sketch, "E186.MirrorCS", {"start": v(-90, -10) * mm, "end": v(-90, 10) * mm});
            skLineSegment(sketch, "E187.MirrorCS", {"start": v(-110, 10) * mm, "end": v(-90, 10) * mm});
            skLineSegment(sketch, "E188.MirrorCS", {"start": v(-135, 10) * mm, "end": v(-115, 10) * mm});
            skLineSegment(sketch, "E189.MirrorCS", {"start": v(-116.8, 2.84) * mm, "end": v(-116.8, -2.84) * mm});
            skLineSegment(sketch, "E190.MirrorCS", {"start": v(-85, -10) * mm, "end": v(-65, -10) * mm});
            skLineSegment(sketch, "E191.MirrorCS", {"start": v(-60, -10) * mm, "end": v(-60, 10) * mm});
            skLineSegment(sketch, "E192.MirrorCS", {"start": v(-110, 0) * mm, "end": v(-90, 0) * mm, "construction": true});
            skLineSegment(sketch, "E193.MirrorCS", {"start": v(-25, 10) * mm, "end": v(-25, -10) * mm, "construction": true});
            skLineSegment(sketch, "E194.MirrorCS", {"start": v(-60, 0) * mm, "end": v(-40, 0) * mm, "construction": true});
            skLineSegment(sketch, "E195.MirrorCS", {"start": v(-90, 10) * mm, "end": v(-110, -10) * mm, "construction": true});
            skLineSegment(sketch, "E196.MirrorCS", {"start": v(-60, 10) * mm, "end": v(-40, 10) * mm});
            skLineSegment(sketch, "E197.MirrorCS", {"start": v(-35, 10) * mm, "end": v(-15, 10) * mm});
            skSolve(sketch);
        }
        {
            var Q0;
            {var subQ7=sQuery(id+"F0.wireOp",EDGE,"E4");Q0=makeQuery(id+"F0.imprint","IMPRINT",FACE,{"disambiguationData":[TD([[makeQuery(id+"F0.imprint","IMPRINT",EDGE,{"derivedFrom":subQ7}),-1.0]])]});}
            var Q1;
            {var subQ3=sQuery(id+"F0.wireOp",EDGE,"E23.MirrorCS");Q1=makeQuery(id+"F0.imprint","IMPRINT",FACE,{"disambiguationData":[TD([[makeQuery(id+"F0.imprint","IMPRINT",EDGE,{"derivedFrom":subQ3}),-1.0]])]});}
            var Q2;
            Q2=makeQuery(id+"F0.imprint","IMPRINT",FACE,{"disambiguationData":[TD([[makeQuery(id+"F0.imprint","IMPRINT",EDGE,{"derivedFrom":sQuery(id+"F0.wireOp",EDGE,"E1")}),-1.0]])]});
            var Q3;
            {var subQ7=sQuery(id+"F0.wireOp",EDGE,"E17");Q3=makeQuery(id+"F0.imprint","IMPRINT",FACE,{"disambiguationData":[TD([[makeQuery(id+"F0.imprint","IMPRINT",EDGE,{"derivedFrom":subQ7}),1.0]])]});}
            var Q4;
            {var subQ0=sQuery(id+"F0.wireOp",EDGE,"E12.MirrorCS");Q4=makeQuery(id+"F0.imprint","IMPRINT",FACE,{"disambiguationData":[TD([[makeQuery(id+"F0.imprint","IMPRINT",EDGE,{"derivedFrom":subQ0}),-1.0]])]});}
            var Q5;
            {var subQ0=sQuery(id+"F0.wireOp",EDGE,"E10.MirrorCS");Q5=makeQuery(id+"F0.imprint","IMPRINT",FACE,{"disambiguationData":[TD([[makeQuery(id+"F0.imprint","IMPRINT",EDGE,{"derivedFrom":subQ0}),1.0]])]});}
            var Q6;
            {var subQ3=sQuery(id+"F0.wireOp",EDGE,"E19.MirrorCS");Q6=makeQuery(id+"F0.imprint","IMPRINT",FACE,{"disambiguationData":[TD([[makeQuery(id+"F0.imprint","IMPRINT",EDGE,{"derivedFrom":subQ3}),1.0]])]});}
            var Q7;
            {var subQ7=sQuery(id+"F0.wireOp",EDGE,"E21.MirrorCS");Q7=makeQuery(id+"F0.imprint","IMPRINT",FACE,{"disambiguationData":[TD([[makeQuery(id+"F0.imprint","IMPRINT",EDGE,{"derivedFrom":subQ7}),1.0]])]});}
            var Q8;
            {var subQ6=sQuery(id+"F0.wireOp",EDGE,"E14.MirrorCS");Q8=makeQuery(id+"F0.imprint","IMPRINT",FACE,{"disambiguationData":[TD([[makeQuery(id+"F0.imprint","IMPRINT",EDGE,{"derivedFrom":subQ6}),1.0]])]});}
            extrude(context, id + "F1", {"entities" : qUnion([Q0, Q1, Q2, Q3, Q4, Q5, Q6, Q7, Q8]), "depth" : 982.5 * mm, "offsetDistance" : 25 * mm});
        }
        {
            var Q0;
            {var subQ8=sQuery(id+"F0.wireOp",EDGE,"E25.1.0.30");Q0=makeQuery(id+"F0.imprint","IMPRINT",FACE,{"disambiguationData":[TD([[makeQuery(id+"F0.imprint","IMPRINT",EDGE,{"derivedFrom":subQ8}),-1.0]])]});}
            var Q1;
            {var subQ8=sQuery(id+"F0.wireOp",EDGE,"E25.1.0.29");Q1=makeQuery(id+"F0.imprint","IMPRINT",FACE,{"disambiguationData":[TD([[makeQuery(id+"F0.imprint","IMPRINT",EDGE,{"derivedFrom":subQ8}),1.0]])]});}
            var Q2;
            {var subQ1=sQuery(id+"F0.wireOp",EDGE,"E25.1.0.0");Q2=makeQuery(id+"F0.imprint","IMPRINT",FACE,{"disambiguationData":[TD([[makeQuery(id+"F0.imprint","IMPRINT",EDGE,{"derivedFrom":subQ1}),-1.0]])]});}
            var Q3;
            Q3=makeQuery(id+"F0.imprint","IMPRINT",FACE,{"disambiguationData":[TD([[makeQuery(id+"F0.imprint","IMPRINT",EDGE,{"derivedFrom":sQuery(id+"F0.wireOp",EDGE,"E25.1.0.24")}),-1.0]])]});
            var Q4;
            {var subQ4=sQuery(id+"F0.wireOp",EDGE,"E25.1.0.5");Q4=makeQuery(id+"F0.imprint","IMPRINT",FACE,{"disambiguationData":[TD([[makeQuery(id+"F0.imprint","IMPRINT",EDGE,{"derivedFrom":subQ4}),1.0]])]});}
            var Q5;
            {var subQ7=sQuery(id+"F0.wireOp",EDGE,"E25.1.0.3");Q5=makeQuery(id+"F0.imprint","IMPRINT",FACE,{"disambiguationData":[TD([[makeQuery(id+"F0.imprint","IMPRINT",EDGE,{"derivedFrom":subQ7}),1.0]])]});}
            var Q6;
            {var subQ2=sQuery(id+"F0.wireOp",EDGE,"E25.1.0.14");Q6=makeQuery(id+"F0.imprint","IMPRINT",FACE,{"disambiguationData":[TD([[makeQuery(id+"F0.imprint","IMPRINT",EDGE,{"derivedFrom":subQ2}),1.0]])]});}
            var Q7;
            {var subQ3=sQuery(id+"F0.wireOp",EDGE,"E25.1.0.23");Q7=makeQuery(id+"F0.imprint","IMPRINT",FACE,{"disambiguationData":[TD([[makeQuery(id+"F0.imprint","IMPRINT",EDGE,{"derivedFrom":subQ3}),-1.0]])]});}
            var Q8;
            {var subQ0=sQuery(id+"F0.wireOp",EDGE,"E25.1.0.22");Q8=makeQuery(id+"F0.imprint","IMPRINT",FACE,{"disambiguationData":[TD([[makeQuery(id+"F0.imprint","IMPRINT",EDGE,{"derivedFrom":subQ0}),-1.0]])]});}
            extrude(context, id + "F2", {"entities" : qUnion([Q0, Q1, Q2, Q3, Q4, Q5, Q6, Q7, Q8]), "depth" : 612 * mm, "offsetDistance" : 25 * mm});
        }
        {
            var Q0;
            {var subQ8=sQuery(id+"F0.wireOp",EDGE,"E25.2.0.30");Q0=makeQuery(id+"F0.imprint","IMPRINT",FACE,{"disambiguationData":[TD([[makeQuery(id+"F0.imprint","IMPRINT",EDGE,{"derivedFrom":subQ8}),-1.0]])]});}
            var Q1;
            {var subQ4=sQuery(id+"F0.wireOp",EDGE,"E25.2.0.5");Q1=makeQuery(id+"F0.imprint","IMPRINT",FACE,{"disambiguationData":[TD([[makeQuery(id+"F0.imprint","IMPRINT",EDGE,{"derivedFrom":subQ4}),1.0]])]});}
            var Q2;
            Q2=makeQuery(id+"F0.imprint","IMPRINT",FACE,{"disambiguationData":[TD([[makeQuery(id+"F0.imprint","IMPRINT",EDGE,{"derivedFrom":sQuery(id+"F0.wireOp",EDGE,"E25.2.0.24")}),-1.0]])]});
            var Q3;
            {var subQ1=sQuery(id+"F0.wireOp",EDGE,"E25.2.0.0");Q3=makeQuery(id+"F0.imprint","IMPRINT",FACE,{"disambiguationData":[TD([[makeQuery(id+"F0.imprint","IMPRINT",EDGE,{"derivedFrom":subQ1}),-1.0]])]});}
            var Q4;
            {var subQ8=sQuery(id+"F0.wireOp",EDGE,"E25.2.0.29");Q4=makeQuery(id+"F0.imprint","IMPRINT",FACE,{"disambiguationData":[TD([[makeQuery(id+"F0.imprint","IMPRINT",EDGE,{"derivedFrom":subQ8}),1.0]])]});}
            var Q5;
            {var subQ0=sQuery(id+"F0.wireOp",EDGE,"E25.2.0.22");Q5=makeQuery(id+"F0.imprint","IMPRINT",FACE,{"disambiguationData":[TD([[makeQuery(id+"F0.imprint","IMPRINT",EDGE,{"derivedFrom":subQ0}),-1.0]])]});}
            var Q6;
            {var subQ3=sQuery(id+"F0.wireOp",EDGE,"E25.2.0.23");Q6=makeQuery(id+"F0.imprint","IMPRINT",FACE,{"disambiguationData":[TD([[makeQuery(id+"F0.imprint","IMPRINT",EDGE,{"derivedFrom":subQ3}),-1.0]])]});}
            var Q7;
            {var subQ7=sQuery(id+"F0.wireOp",EDGE,"E25.2.0.3");Q7=makeQuery(id+"F0.imprint","IMPRINT",FACE,{"disambiguationData":[TD([[makeQuery(id+"F0.imprint","IMPRINT",EDGE,{"derivedFrom":subQ7}),1.0]])]});}
            var Q8;
            {var subQ2=sQuery(id+"F0.wireOp",EDGE,"E25.2.0.14");Q8=makeQuery(id+"F0.imprint","IMPRINT",FACE,{"disambiguationData":[TD([[makeQuery(id+"F0.imprint","IMPRINT",EDGE,{"derivedFrom":subQ2}),1.0]])]});}
            extrude(context, id + "F3", {"entities" : qUnion([Q0, Q1, Q2, Q3, Q4, Q5, Q6, Q7, Q8]), "depth" : 200 * mm, "offsetDistance" : 25 * mm});
        }
        {
            var Q0;
            {var subQ3=sQuery(id+"F0.wireOp",EDGE,"E106.MirrorCS");Q0=makeQuery(id+"F0.imprint","IMPRINT",FACE,{"disambiguationData":[TD([[makeQuery(id+"F0.imprint","IMPRINT",EDGE,{"derivedFrom":subQ3}),-1.0]])]});}
            var Q1;
            {var subQ3=sQuery(id+"F0.wireOp",EDGE,"E140.MirrorCS");Q1=makeQuery(id+"F0.imprint","IMPRINT",FACE,{"disambiguationData":[TD([[makeQuery(id+"F0.imprint","IMPRINT",EDGE,{"derivedFrom":subQ3}),-1.0]])]});}
            var Q2;
            Q2=makeQuery(id+"F0.imprint","IMPRINT",FACE,{"disambiguationData":[TD([[makeQuery(id+"F0.imprint","IMPRINT",EDGE,{"derivedFrom":sQuery(id+"F0.wireOp",EDGE,"E30.MirrorC")}),1.0]])]});
            var Q3;
            {var subQ1=sQuery(id+"F0.wireOp",EDGE,"E62.MirrorCS");Q3=makeQuery(id+"F0.imprint","IMPRINT",FACE,{"disambiguationData":[TD([[makeQuery(id+"F0.imprint","IMPRINT",EDGE,{"derivedFrom":subQ1}),1.0]])]});}
            var Q4;
            {var subQ1=sQuery(id+"F0.wireOp",EDGE,"E38.MirrorCS");Q4=makeQuery(id+"F0.imprint","IMPRINT",FACE,{"disambiguationData":[TD([[makeQuery(id+"F0.imprint","IMPRINT",EDGE,{"derivedFrom":subQ1}),1.0]])]});}
            var Q5;
            {var subQ8=sQuery(id+"F0.wireOp",EDGE,"E27.MirrorCS");Q5=makeQuery(id+"F0.imprint","IMPRINT",FACE,{"disambiguationData":[TD([[makeQuery(id+"F0.imprint","IMPRINT",EDGE,{"derivedFrom":subQ8}),-1.0]])]});}
            var Q6;
            {var subQ0=sQuery(id+"F0.wireOp",EDGE,"E104.MirrorCS");Q6=makeQuery(id+"F0.imprint","IMPRINT",FACE,{"disambiguationData":[TD([[makeQuery(id+"F0.imprint","IMPRINT",EDGE,{"derivedFrom":subQ0}),-1.0]])]});}
            var Q7;
            {var subQ1=sQuery(id+"F0.wireOp",EDGE,"E46.MirrorCS");Q7=makeQuery(id+"F0.imprint","IMPRINT",FACE,{"disambiguationData":[TD([[makeQuery(id+"F0.imprint","IMPRINT",EDGE,{"derivedFrom":subQ1}),1.0]])]});}
            var Q8;
            {var subQ1=sQuery(id+"F0.wireOp",EDGE,"E64.MirrorCS");Q8=makeQuery(id+"F0.imprint","IMPRINT",FACE,{"disambiguationData":[TD([[makeQuery(id+"F0.imprint","IMPRINT",EDGE,{"derivedFrom":subQ1}),1.0]])]});}
            extrude(context, id + "F4", {"entities" : qUnion([Q0, Q1, Q2, Q3, Q4, Q5, Q6, Q7, Q8]), "depth" : 120 * mm, "offsetDistance" : 25 * mm});
        }
        {
            var Q0;
            {var subQ1=sQuery(id+"F0.wireOp",EDGE,"E89.MirrorCS");Q0=makeQuery(id+"F0.imprint","IMPRINT",FACE,{"disambiguationData":[TD([[makeQuery(id+"F0.imprint","IMPRINT",EDGE,{"derivedFrom":subQ1}),1.0]])]});}
            var Q1;
            Q1=makeQuery(id+"F0.imprint","IMPRINT",FACE,{"disambiguationData":[TD([[makeQuery(id+"F0.imprint","IMPRINT",EDGE,{"derivedFrom":sQuery(id+"F0.wireOp",EDGE,"E28.MirrorC")}),1.0]])]});
            var Q2;
            {var subQ1=sQuery(id+"F0.wireOp",EDGE,"E37.MirrorCS");Q2=makeQuery(id+"F0.imprint","IMPRINT",FACE,{"disambiguationData":[TD([[makeQuery(id+"F0.imprint","IMPRINT",EDGE,{"derivedFrom":subQ1}),1.0]])]});}
            var Q3;
            {var subQ0=sQuery(id+"F0.wireOp",EDGE,"E99.MirrorCS");Q3=makeQuery(id+"F0.imprint","IMPRINT",FACE,{"disambiguationData":[TD([[makeQuery(id+"F0.imprint","IMPRINT",EDGE,{"derivedFrom":subQ0}),1.0]])]});}
            var Q4;
            {var subQ4=sQuery(id+"F0.wireOp",EDGE,"E88.MirrorCS");Q4=makeQuery(id+"F0.imprint","IMPRINT",FACE,{"disambiguationData":[TD([[makeQuery(id+"F0.imprint","IMPRINT",EDGE,{"derivedFrom":subQ4}),-1.0]])]});}
            var Q5;
            {var subQ0=sQuery(id+"F0.wireOp",EDGE,"E118.MirrorCS");Q5=makeQuery(id+"F0.imprint","IMPRINT",FACE,{"disambiguationData":[TD([[makeQuery(id+"F0.imprint","IMPRINT",EDGE,{"derivedFrom":subQ0}),1.0]])]});}
            var Q6;
            {var subQ1=sQuery(id+"F0.wireOp",EDGE,"E40.MirrorCS");Q6=makeQuery(id+"F0.imprint","IMPRINT",FACE,{"disambiguationData":[TD([[makeQuery(id+"F0.imprint","IMPRINT",EDGE,{"derivedFrom":subQ1}),1.0]])]});}
            var Q7;
            {var subQ4=sQuery(id+"F0.wireOp",EDGE,"E35.MirrorCS");Q7=makeQuery(id+"F0.imprint","IMPRINT",FACE,{"disambiguationData":[TD([[makeQuery(id+"F0.imprint","IMPRINT",EDGE,{"derivedFrom":subQ4}),-1.0]])]});}
            var Q8;
            {var subQ1=sQuery(id+"F0.wireOp",EDGE,"E44.MirrorCS");Q8=makeQuery(id+"F0.imprint","IMPRINT",FACE,{"disambiguationData":[TD([[makeQuery(id+"F0.imprint","IMPRINT",EDGE,{"derivedFrom":subQ1}),-1.0]])]});}
            extrude(context, id + "F5", {"entities" : qUnion([Q0, Q1, Q2, Q3, Q4, Q5, Q6, Q7, Q8]), "depth" : 40 * mm, "offsetDistance" : 25 * mm});
        }
        {
            var Q0;
            {var subQ1=sQuery(id+"F0.wireOp",EDGE,"E70.MirrorCS");Q0=makeQuery(id+"F0.imprint","IMPRINT",FACE,{"disambiguationData":[TD([[makeQuery(id+"F0.imprint","IMPRINT",EDGE,{"derivedFrom":subQ1}),1.0]])]});}
            var Q1;
            {var subQ0=sQuery(id+"F0.wireOp",EDGE,"E100.MirrorCS");Q1=makeQuery(id+"F0.imprint","IMPRINT",FACE,{"disambiguationData":[TD([[makeQuery(id+"F0.imprint","IMPRINT",EDGE,{"derivedFrom":subQ0}),-1.0]])]});}
            var Q2;
            Q2=makeQuery(id+"F0.imprint","IMPRINT",FACE,{"disambiguationData":[TD([[makeQuery(id+"F0.imprint","IMPRINT",EDGE,{"derivedFrom":sQuery(id+"F0.wireOp",EDGE,"E32.MirrorC")}),1.0]])]});
            var Q3;
            {var subQ8=sQuery(id+"F0.wireOp",EDGE,"E36.MirrorCS");Q3=makeQuery(id+"F0.imprint","IMPRINT",FACE,{"disambiguationData":[TD([[makeQuery(id+"F0.imprint","IMPRINT",EDGE,{"derivedFrom":subQ8}),1.0]])]});}
            var Q4;
            {var subQ7=sQuery(id+"F0.wireOp",EDGE,"E74.MirrorCS");Q4=makeQuery(id+"F0.imprint","IMPRINT",FACE,{"disambiguationData":[TD([[makeQuery(id+"F0.imprint","IMPRINT",EDGE,{"derivedFrom":subQ7}),1.0]])]});}
            var Q5;
            {var subQ6=sQuery(id+"F0.wireOp",EDGE,"E39.MirrorCS");Q5=makeQuery(id+"F0.imprint","IMPRINT",FACE,{"disambiguationData":[TD([[makeQuery(id+"F0.imprint","IMPRINT",EDGE,{"derivedFrom":subQ6}),-1.0]])]});}
            var Q6;
            {var subQ1=sQuery(id+"F0.wireOp",EDGE,"E114.MirrorCS");Q6=makeQuery(id+"F0.imprint","IMPRINT",FACE,{"disambiguationData":[TD([[makeQuery(id+"F0.imprint","IMPRINT",EDGE,{"derivedFrom":subQ1}),-1.0]])]});}
            var Q7;
            {var subQ5=sQuery(id+"F0.wireOp",EDGE,"E57.MirrorCS");Q7=makeQuery(id+"F0.imprint","IMPRINT",FACE,{"disambiguationData":[TD([[makeQuery(id+"F0.imprint","IMPRINT",EDGE,{"derivedFrom":subQ5}),1.0]])]});}
            var Q8;
            {var subQ5=sQuery(id+"F0.wireOp",EDGE,"E84.MirrorCS");Q8=makeQuery(id+"F0.imprint","IMPRINT",FACE,{"disambiguationData":[TD([[makeQuery(id+"F0.imprint","IMPRINT",EDGE,{"derivedFrom":subQ5}),1.0]])]});}
            extrude(context, id + "F6", {"entities" : qUnion([Q0, Q1, Q2, Q3, Q4, Q5, Q6, Q7, Q8]), "depth" : 100 * mm, "offsetDistance" : 25 * mm});
        }
    });
